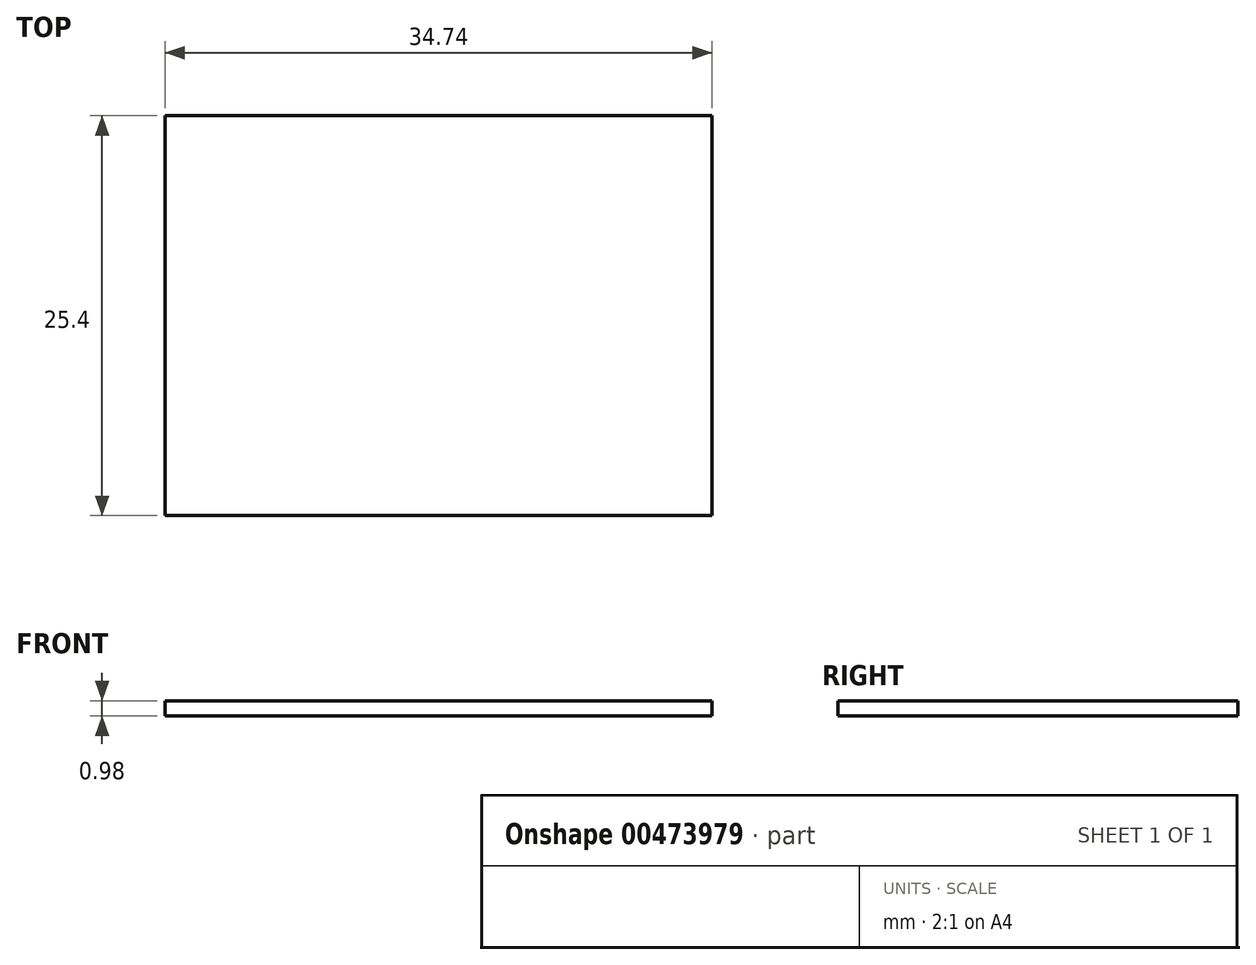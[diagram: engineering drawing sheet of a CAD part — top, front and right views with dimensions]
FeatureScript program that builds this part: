
annotation { "Feature Type Name" : "Feature", "Feature Type Description" : "" }
export const myFeature = defineFeature(function(context is Context, id is Id, definition is map)
    precondition{}
    {
        {
            var Q0;
            Q0=qCreatedBy(makeId("Front.planeOp"),FACE);
            var sketch = newSketch(context, id + "F0", { "sketchPlane" : qUnion([Q0])});
            skLineSegment(sketch, "E0.bottom", {"start": v(-17.37, 0.5) * mm, "end": v(17.37, 0.5) * mm});
            skLineSegment(sketch, "E0.top", {"start": v(-17.37, -0.5) * mm, "end": v(17.37, -0.5) * mm});
            skLineSegment(sketch, "E0.left", {"start": v(-17.37, 0.5) * mm, "end": v(-17.37, -0.5) * mm});
            skLineSegment(sketch, "E0.right", {"start": v(17.37, 0.5) * mm, "end": v(17.37, -0.5) * mm});
            skPoint(sketch, "E0.middle", {"position": v(0, 0) * mm});
            skArc(sketch, "E1", {"start": v(17.37, -0.5) * mm, "mid": v(3.92, -7.11) * mm, "end": v(0.95, -21.81) * mm});
            skArc(sketch, "E2", {"start": v(-2.22, -15.58) * mm, "mid": v(-6.68, -4.9) * mm, "end": v(-17.37, -0.5) * mm});
            skArc(sketch, "E3", {"start": v(-17.37, 0.5) * mm, "mid": v(-3.95, 7.7) * mm, "end": v(-2.56, 22.88) * mm});
            skArc(sketch, "E4", {"start": v(6.97, 28.63) * mm, "mid": v(2.37, 10.94) * mm, "end": v(17.37, 0.5) * mm});
            skSolve(sketch);
        }
        {
            var Q0;
            Q0 = qSketchRegion(id + "F0", true);
            extrude(context, id + "F1", {"entities" : qUnion([Q0]), "endBound" : BoundingType.SYMMETRIC, "depth" : 25.4 * mm});
        }
    });
